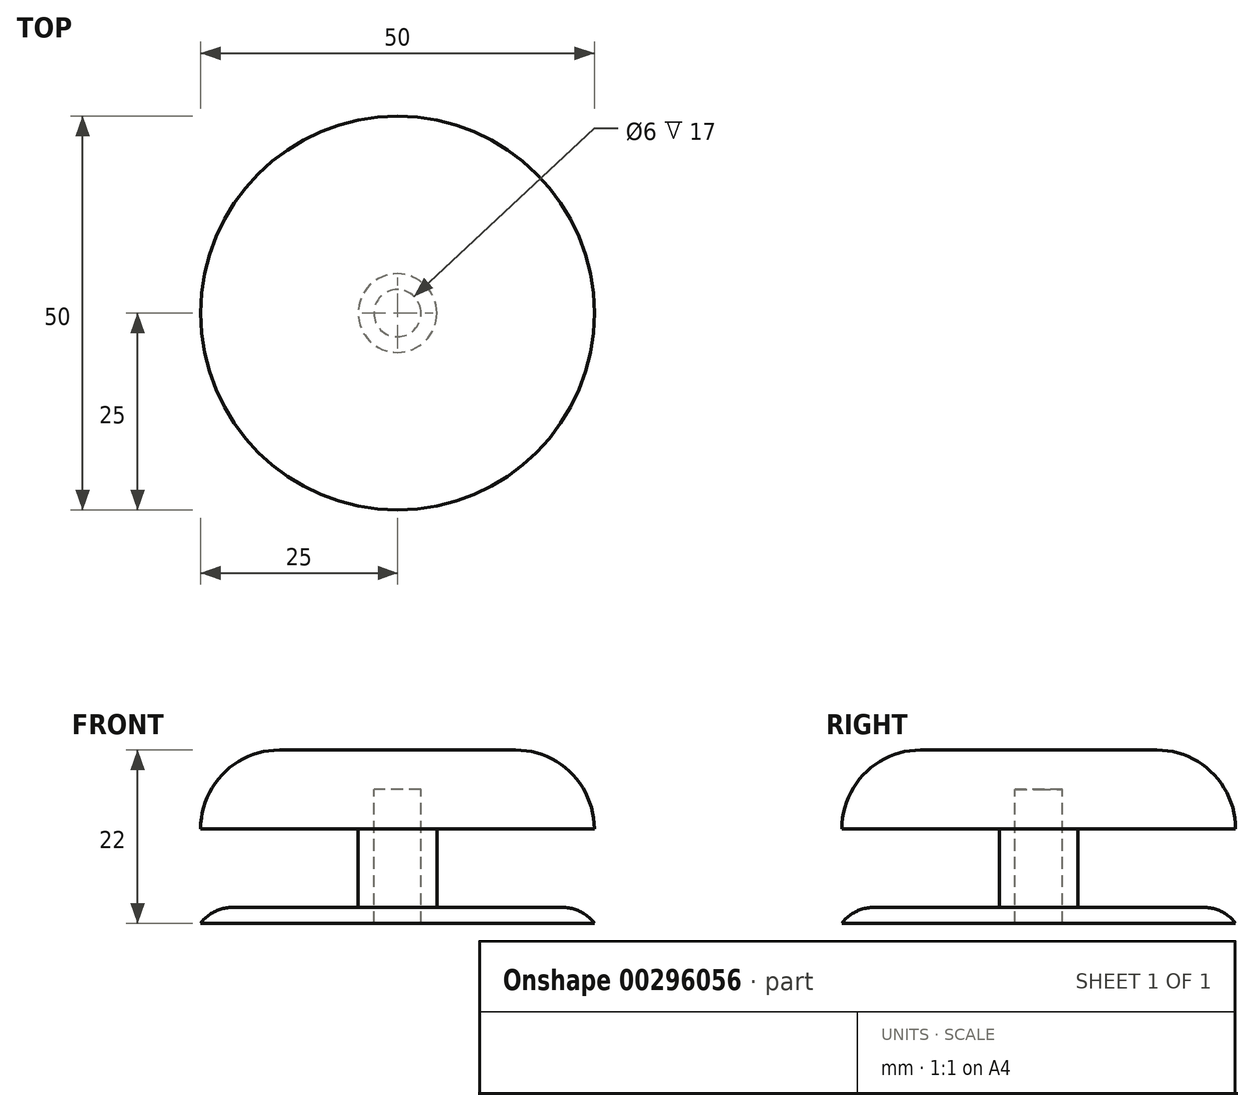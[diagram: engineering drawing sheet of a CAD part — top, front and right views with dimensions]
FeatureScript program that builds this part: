
annotation { "Feature Type Name" : "Feature", "Feature Type Description" : "" }
export const myFeature = defineFeature(function(context is Context, id is Id, definition is map)
    precondition{}
    {
        {
            var Q0;
            Q0=qCreatedBy(makeId("Top.planeOp"),FACE);
            var sketch = newSketch(context, id + "F0", { "sketchPlane" : qUnion([Q0])});
            skCircle(sketch, "E0", {"center": v(0, 0) * mm, "radius": 25 * mm});
            skCircle(sketch, "E1", {"center": v(0, 0) * mm, "radius": 11 * mm});
            skCircle(sketch, "E2", {"center": v(0, 0) * mm, "radius": 5 * mm});
            skCircle(sketch, "E3", {"center": v(0, 0) * mm, "radius": 3 * mm});
            skCircle(sketch, "E4.0", {"center": v(0, 0) * mm, "radius": 13 * mm});
            skCircle(sketch, "E5.0", {"center": v(0, 0) * mm, "radius": 8 * mm});
            skSolve(sketch);
        }
        {
            var Q0;
            Q0=makeQuery(id+"F0.imprint","IMPRINT",FACE,{"disambiguationData":[TD([[makeQuery(id+"F0.imprint","IMPRINT",EDGE,{"derivedFrom":sQuery(id+"F0.wireOp",EDGE,"E0")}),1.0]])]});
            var Q1;
            Q1=makeQuery(id+"F0.imprint","IMPRINT",FACE,{"disambiguationData":[TD([[makeQuery(id+"F0.imprint","IMPRINT",EDGE,{"derivedFrom":sQuery(id+"F0.wireOp",EDGE,"E1")}),-1.0]])]});
            var Q2;
            Q2=makeQuery(id+"F0.imprint","IMPRINT",FACE,{"disambiguationData":[TD([[makeQuery(id+"F0.imprint","IMPRINT",EDGE,{"derivedFrom":sQuery(id+"F0.wireOp",EDGE,"E1")}),1.0]])]});
            var Q3;
            Q3=makeQuery(id+"F0.imprint","IMPRINT",FACE,{"disambiguationData":[TD([[makeQuery(id+"F0.imprint","IMPRINT",EDGE,{"derivedFrom":sQuery(id+"F0.wireOp",EDGE,"E2")}),-1.0]])]});
            var Q4;
            Q4=makeQuery(id+"F0.imprint","IMPRINT",FACE,{"disambiguationData":[TD([[makeQuery(id+"F0.imprint","IMPRINT",EDGE,{"derivedFrom":sQuery(id+"F0.wireOp",EDGE,"E2")}),1.0]])]});
            extrude(context, id + "F1", {"entities" : qUnion([Q0, Q1, Q2, Q3, Q4]), "oppositeDirection" : true, "depth" : 2 * mm});
        }
        {
            var Q0;
            Q0=makeQuery(id+"F0.imprint","IMPRINT",FACE,{"disambiguationData":[TD([[makeQuery(id+"F0.imprint","IMPRINT",EDGE,{"derivedFrom":sQuery(id+"F0.wireOp",EDGE,"E1")}),-1.0]])]});
            extrude(context, id + "F2", {"entities" : qUnion([Q0]), "operationType" : NewBodyOperationType.ADD, "depth" : 10 * mm});
        }
        {
            var Q0;
            Q0=makeQuery(id+"F0.imprint","IMPRINT",FACE,{"disambiguationData":[TD([[makeQuery(id+"F0.imprint","IMPRINT",EDGE,{"derivedFrom":sQuery(id+"F0.wireOp",EDGE,"E2")}),-1.0]])]});
            extrude(context, id + "F3", {"entities" : qUnion([Q0]), "operationType" : NewBodyOperationType.ADD, "depth" : 4 * mm});
        }
        {
            var Q0;
            Q0=makeQuery(id+"F1.opExtrude","CAP_EDGE",EDGE,{"disambiguationData":[OSD([sQuery(id+"F0.wireOp",EDGE,"E0")])],"isStart":true});
            fillet(context, id + "F4", {"entities" : qUnion([Q0]), "radius" : 5.08 * mm, "tangentPropagation" : true, "allowEdgeOverflow" : false});
        }
        {
            var Q0;
            Q0=makeQuery(id+"F0.imprint","IMPRINT",FACE,{"disambiguationData":[TD([[makeQuery(id+"F0.imprint","IMPRINT",EDGE,{"derivedFrom":sQuery(id+"F0.wireOp",EDGE,"E2")}),1.0]])]});
            extrude(context, id + "F5", {"entities" : qUnion([Q0]), "depth" : 20 * mm});
        }
        {
            var Q0;
            Q0=makeQuery(id+"F0.imprint","IMPRINT",FACE,{"disambiguationData":[TD([[makeQuery(id+"F0.imprint","IMPRINT",EDGE,{"derivedFrom":sQuery(id+"F0.wireOp",EDGE,"E2")}),-1.0]])]});
            var Q1;
            Q1=makeQuery(id+"F0.imprint","IMPRINT",FACE,{"disambiguationData":[TD([[makeQuery(id+"F0.imprint","IMPRINT",EDGE,{"derivedFrom":sQuery(id+"F0.wireOp",EDGE,"E1")}),1.0]])]});
            var Q2;
            Q2=makeQuery(id+"F0.imprint","IMPRINT",FACE,{"disambiguationData":[TD([[makeQuery(id+"F0.imprint","IMPRINT",EDGE,{"derivedFrom":sQuery(id+"F0.wireOp",EDGE,"E1")}),-1.0]])]});
            var Q3;
            Q3=makeQuery(id+"F0.imprint","IMPRINT",FACE,{"disambiguationData":[TD([[makeQuery(id+"F0.imprint","IMPRINT",EDGE,{"derivedFrom":sQuery(id+"F0.wireOp",EDGE,"E0")}),1.0]])]});
            extrude(context, id + "F6", {"entities" : qUnion([Q0, Q1, Q2, Q3]), "operationType" : NewBodyOperationType.ADD, "depth" : 20 * mm});
        }
        {
            var Q0;
            Q0 = qSketchRegion(id + "F0", true);
            var Q1;
            Q1=makeQuery(id+"F0.imprint","IMPRINT",FACE,{"disambiguationData":[TD([[makeQuery(id+"F0.imprint","IMPRINT",EDGE,{"derivedFrom":sQuery(id+"F0.wireOp",EDGE,"E1")}),-1.0]])]});
            var Q2;
            Q2=makeQuery(id+"F0.imprint","IMPRINT",FACE,{"disambiguationData":[TD([[makeQuery(id+"F0.imprint","IMPRINT",EDGE,{"derivedFrom":sQuery(id+"F0.wireOp",EDGE,"E1")}),1.0]])]});
            var Q3;
            Q3=makeQuery(id+"F0.imprint","IMPRINT",FACE,{"disambiguationData":[TD([[makeQuery(id+"F0.imprint","IMPRINT",EDGE,{"derivedFrom":sQuery(id+"F0.wireOp",EDGE,"E2")}),-1.0]])]});
            extrude(context, id + "F7", {"entities" : qUnion([Q0, Q1, Q2, Q3]), "operationType" : NewBodyOperationType.REMOVE, "depth" : 10 * mm});
        }
        {
            var Q0;
            Q0=makeQuery(id+"F6.opExtrude","CAP_EDGE",EDGE,{"disambiguationData":[OSD([sQuery(id+"F0.wireOp",EDGE,"E0")])],"isStart":false});
            fillet(context, id + "F8", {"entities" : qUnion([Q0]), "radius" : 10 * mm, "tangentPropagation" : true, "allowEdgeOverflow" : false});
        }
        {
            var Q0;
            Q0=makeQuery(id+"F0.imprint","IMPRINT",FACE,{"disambiguationData":[TD([[makeQuery(id+"F0.imprint","IMPRINT",EDGE,{"derivedFrom":sQuery(id+"F0.wireOp",EDGE,"E3")}),1.0]])]});
            extrude(context, id + "F9", {"entities" : qUnion([Q0]), "operationType" : NewBodyOperationType.ADD, "depth" : 20 * mm, "hasSecondDirection" : true, "secondDirectionOppositeDirection" : false, "secondDirectionDepth" : 15 * mm});
        }
    });
